# Revit family: Lil_L
name_source: partatom
category: Plumbing Fixtures
units: mm (PartAtom-declared; Revit-internal decimal feet)

## family parameters
Always vertical = Yes
Cut with Voids When Loaded = No
Part Type = Normal
Room Calculation Point = No
Round Connector Dimension = Use Diameter
Shared = No
Work Plane-Based = No

## types (2) — shared parameters
BOTTOM 1 = 9"
C = 3 1/2"
F = 2"
F/2 = 1"
F2 = 13/16"
FULL DIM = 6"
Manufacturer = MIFAB
Material = Polyethylene, High Density
Pressure Drop = 0.00 psi
TOP THK = 1 1/2"
TOP1 = 1 1/2"
URL = www.mifab.com

## per-type parameters (varying)
| type | A | A+1 | B | D | Description | E | Mechanical Flow | Model | top 2 |
| Lil-7-L | 19 1/2" | 10 1/2" | 15 1/2" | 9" | 7GPM Lil Max HDPE Plaster Interceptor | 12 1/2" | 7 GPM | MI-G-1-PL-PSB-FSCR | 2" |
| Lil-15-L | 23" | 12 5/16" | 17 1/2" | 13 1/4" | 15GPM Lil Max HDPE Plaster Interceptor | 16 3/4" | 15 GPM | MI-G-3-PL-PSB-FSCR | 3 1/8" |

## geometry (parser evidence)
native form markers: Sweep x2
no freeform markers — native parametric forms only
